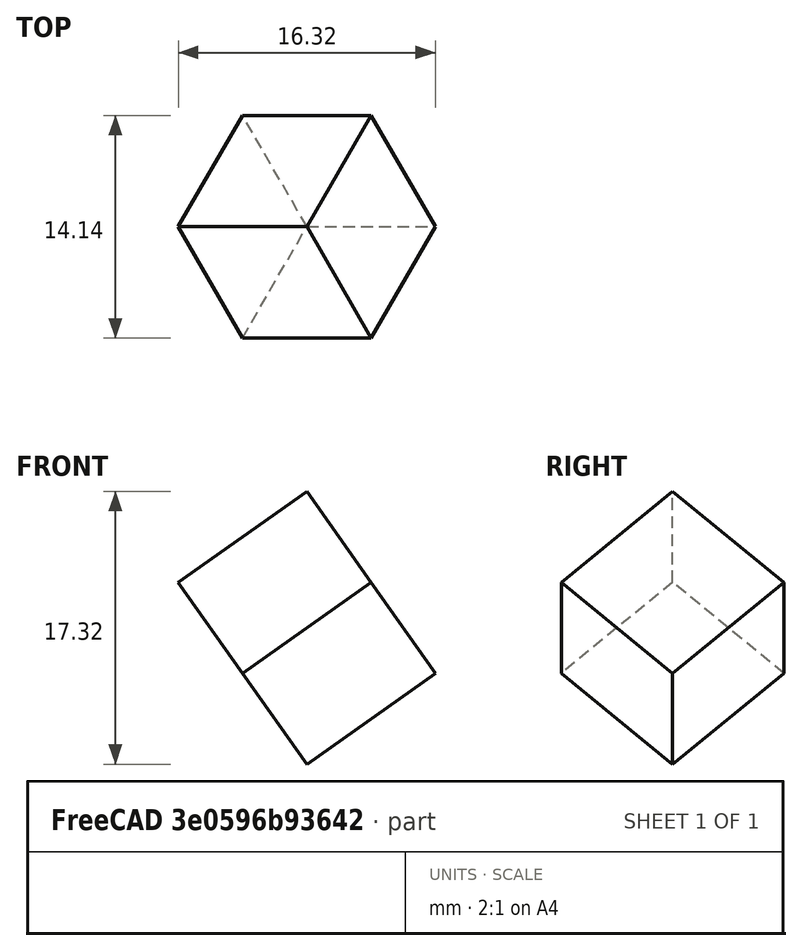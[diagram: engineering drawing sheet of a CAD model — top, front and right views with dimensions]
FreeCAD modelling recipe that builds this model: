
FCSTD DOCUMENT  (FreeCAD 0.19R17089 +1543 (Git))
Label: cube-on-corner
License: All rights reserved
LicenseURL: http://en.wikipedia.org/wiki/All_rights_reserved
objects: Sketcher::SketchObject×3, App::DocumentObjectGroup×1, PartDesign::Pad×1, PartDesign::Body×1
note: 6 computed .brp shape members not serialized (recipe doc carries the construction recipe); baked Part::Feature solids carry a one-line shape summary decoded from their .brp

FEATURE [Sketcher::SketchObject] Sketch
  Placement = pos=(0,0,0) rot=(-1,0,0;4.71239rad)
  sketch-geometry (3):
    g0: LineSegment StartX=0 StartY=-9e-16 StartZ=0 EndX=7 EndY=0 EndZ=0
    g1: LineSegment StartX=7 StartY=0 StartZ=0 EndX=7 EndY=5 EndZ=0
    g2: LineSegment StartX=7 StartY=5 StartZ=0 EndX=0 EndY=-9e-16 EndZ=0
  constraints (10):
    c: Coincident(g-1,g0)
    c: PointOnObject(g0,g-1)
    c: Coincident(g0,g1)
    c: Vertical(g1)
    c: Coincident(g1,g2)
    c: Coincident(g2,g0)
    c: Distance(g1) = 5  'HSL'
    c: Distance(g0) = 7  'HCDL'
    c: Angle(g0,g2) = 0.620249
    c: Angle(g2,g-2) = 0.950547
FEATURE [Sketcher::SketchObject] Sketch001
  Placement = pos=(0,0,0) rot=(-1,0,0;4.71239rad)
  expr: Constraints[2] = Sketch.Constraints.HCDL * 2 + 15mm
  sketch-geometry (1):
    g0: LineSegment StartX=0 StartY=14.5 StartZ=0 EndX=0 EndY=-14.5 EndZ=0
  constraints (3):
    c: PointOnObject(g0,g-2)
    c: Symmetric(g0,g0,g-1)
    c: DistanceY(g0,g0) = 29
FEATURE [App::DocumentObjectGroup] Group  label="Repository"
  Group = -> [Sketch,Sketch001]
FEATURE [Sketcher::SketchObject] Sketch002
  MapMode = 5
  Support = -> [XY_Plane]
  expr: .Constraints.SL = Sketch.Constraints.HSL * 2
  sketch-geometry (5):
    g0: LineSegment StartX=7.07107 StartY=-9e-16 StartZ=0 EndX=-1.0694e-12 EndY=7.07107 EndZ=0
    g1: LineSegment StartX=-1.0694e-12 StartY=7.07107 StartZ=0 EndX=-7.07107 EndY=-3.633e-13 EndZ=0
    g2: LineSegment StartX=-7.07107 StartY=-3.633e-13 StartZ=0 EndX=6.48e-14 EndY=-7.07107 EndZ=0
    g3: LineSegment StartX=6.48e-14 StartY=-7.07107 StartZ=0 EndX=7.07107 EndY=-9e-16 EndZ=0
    g4: Circle [constr] CenterX=0 CenterY=0 CenterZ=0 NormalX=0 NormalY=0 NormalZ=1 AngleXU=0 Radius=7.07107
  constraints (14):
    c: Coincident(g0,g1)
    c: Coincident(g1,g2)
    c: Coincident(g2,g3)
    c: Coincident(g3,g0)
    c: Equal(g0,g1)
    c: Equal(g0,g2)
    c: Equal(g0,g3)
    c: PointOnObject(g0,g4)
    c: PointOnObject(g1,g4)
    c: PointOnObject(g2,g4)
    c: PointOnObject(g3,g4)
    c: Coincident(g4,g-1)
    c: PointOnObject(g3,g-1)
    c: Distance(g0) = 10  'SL'
FEATURE [PartDesign::Pad] Pad
  ClaimChildren = false
  Length = 10
  Length2 = 100
  Midplane = true
  Profile = -> Sketch002
  Type = 0
FEATURE [PartDesign::Body] Body
  Group = -> [Sketch002,Pad]
  Origin = -> Origin
  Placement = pos=(0,0,0) rot=(0,1,0;0.955317rad)
  Tip = -> Pad
  expr: .Placement.Rotation.Angle = 90deg - atan(sqrt(1 / 2))
